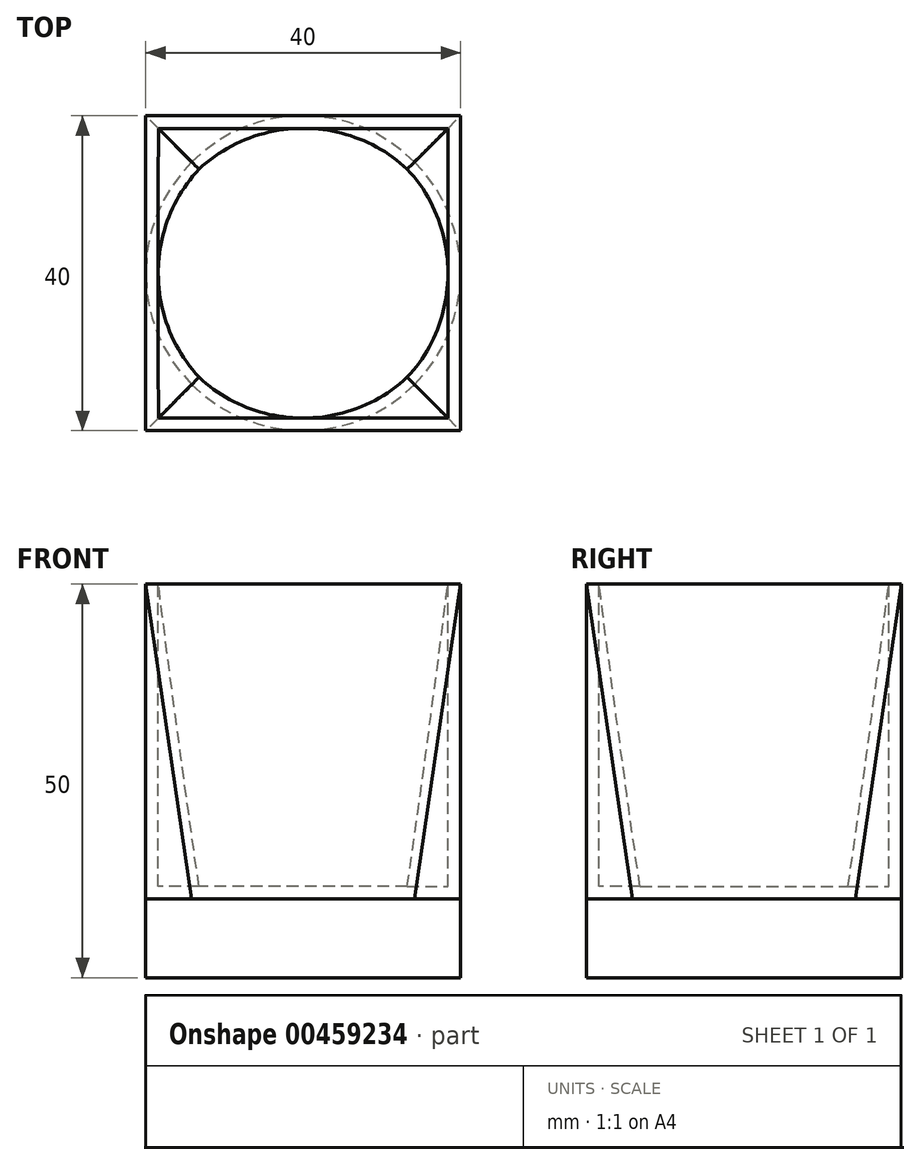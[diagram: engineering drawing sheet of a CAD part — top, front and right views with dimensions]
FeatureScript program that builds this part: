
annotation { "Feature Type Name" : "Feature", "Feature Type Description" : "" }
export const myFeature = defineFeature(function(context is Context, id is Id, definition is map)
    precondition{}
    {
        {
            var Q0;
            Q0=qCreatedBy(makeId("Top.planeOp"),FACE);
            var sketch = newSketch(context, id + "F0", { "sketchPlane" : qUnion([Q0])});
            skCircle(sketch, "E0", {"center": v(0, 0) * mm, "radius": 20 * mm});
            skSolve(sketch);
        }
        {
            var Q0;
            Q0=qCreatedBy(makeId("Top.planeOp"),FACE);
            cPlane(context, id + "F1", {"entities" : qUnion([Q0]), "cplaneType" : CPlaneType.OFFSET, "offset" : 40 * mm, "width" : 150 * mm, "height" : 150 * mm});
        }
        {
            var Q0;
            Q0=qCreatedBy(id+"F1.planeOp",FACE);
            var sketch = newSketch(context, id + "F2", { "sketchPlane" : qUnion([Q0])});
            skLineSegment(sketch, "E1.bottom", {"start": v(-20, 20) * mm, "end": v(20, 20) * mm});
            skLineSegment(sketch, "E1.top", {"start": v(-20, -20) * mm, "end": v(20, -20) * mm});
            skLineSegment(sketch, "E1.left", {"start": v(-20, 20) * mm, "end": v(-20, -20) * mm});
            skLineSegment(sketch, "E1.right", {"start": v(20, 20) * mm, "end": v(20, -20) * mm});
            skPoint(sketch, "E1.middle", {"position": v(0, 0) * mm});
            skSolve(sketch);
        }
        {
            var Q0;
            Q0=makeQuery(id+"F0.imprint","IMPRINT",FACE,{"disambiguationData":[TD([[makeQuery(id+"F0.imprint","IMPRINT",EDGE,{"derivedFrom":sQuery(id+"F0.wireOp",EDGE,"E0")}),1.0]])]});
            var Q1;
            Q1=makeQuery(id+"F2.imprint","IMPRINT",FACE,{"disambiguationData":[TD([[makeQuery(id+"F2.imprint","IMPRINT",EDGE,{"derivedFrom":sQuery(id+"F2.wireOp",EDGE,"E1.bottom")}),-1.0]])]});
            loft(context, id + "F3", {"sheetProfilesArray" : [{ "sheetProfileEntities" : qUnion([Q0]) }, { "sheetProfileEntities" : qUnion([Q1]) }]});
        }
        {
            var Q0;
            Q0=makeQuery(id+"F3.opLoft","CAP_FACE",FACE,{"disambiguationData":[OSD([makeQuery(id+"F2.imprint","IMPRINT",FACE,{"disambiguationData":[TD([[makeQuery(id+"F2.imprint","IMPRINT",EDGE,{"derivedFrom":sQuery(id+"F2.wireOp",EDGE,"E1.bottom")}),-1.0]])]})])],"isStart":true});
            shell(context, id + "F4", {"entities" : qUnion([Q0]), "thickness" : 1.6 * mm});
        }
        {
            var Q0;
            Q0=makeQuery(id+"F0.imprint","IMPRINT",FACE,{"disambiguationData":[TD([[makeQuery(id+"F0.imprint","IMPRINT",EDGE,{"derivedFrom":sQuery(id+"F0.wireOp",EDGE,"E0")}),1.0]])]});
            extrude(context, id + "F5", {"entities" : qUnion([Q0]), "oppositeDirection" : true, "depth" : 10 * mm});
        }
    });
